# Revit family: OPTIMA_Compact_P_MM_DN15_2,5_RFA_2019
name_source: partatom
category: Pipe Accessories
units: mm (PartAtom-declared; Revit-internal decimal feet)

## family parameters
Always vertical = Yes
Cut with Voids When Loaded = No
Part Type = Valve - Breaks Into
Round Connector Dimension = Use Diameter
Shared = No
Work Plane-Based = No

## types (4) — shared parameters
BBVIS = No
CAT = No
Description = Armatura pro regulaci průtoku, omezení průtoku a stabilizaci tlakové diference
ENBL350 = No
H = 83 mm  [stored 0.27231 ft]
HH = 80 mm  [stored 0.262467 ft]
L = 36 mm  [stored 0.11811 ft]
L2 = 44 mm
L2D = 36 mm  [stored 0.11811 ft]
L2D_Min = 30 mm  [stored 0.0984252 ft]
L3 = 19 mm  [stored 0.062336 ft]
L4 = 13 mm  [stored 0.0426509 ft]
LLDAndHLD = Yes
LLDONLY = Yes
MC Enable LOD 200 = No
MC Enable LOD 350 = No
Manufacturer = Hydronic Systems Prague s.r.o.
QmdConnectorList = 301;D;302;D
R2 = 19 mm  [stored 0.062336 ft]
R2__ve = -19 mm  [stored -0.062336 ft]
R3 = 11 mm
R4 = 13 mm  [stored 0.0426509 ft]
R5 = 14 mm  [stored 0.0459318 ft]
R7 = 5 mm  [stored 0.0164042 ft]
Type Comments = vnější závit; PN25; 0~120°C, dpmax=800kPa; bez měřicích vsuvek
URL = www.hydronic.cz
VIS0 = No
Z1 = 17 mm
Z2 = 8 mm  [stored 0.0262467 ft]
Z3 = 13 mm  [stored 0.0426509 ft]
Z4 = 18 mm
Z6 = 5 mm  [stored 0.0164042 ft]
magiPartTypeId = 304
magiProductFamilyId = 5ce2593e541b4756b7958a6220b877

## per-type parameters (varying)
| type | D | DT2 | MC Product Code | R1 | TL | TLT2 | W2D | X1 | X2 | Z5 | magiProductId |
| OPTIMA Compact P DN15 M-M 2.5mm | 15 mm | 8 mm  [stored 0.0262467 ft] | 53-4100  (1/2" M-M; 2.5mm; Qmin~Qmax při dps=5kPa = 93~482 l/h; Qmin~Qmax při dps=10kPa = 73~378 l/h; kvs=1,3) | 7 mm  [stored 0.0229659 ft] | 65 mm  [stored 0.213255 ft] | 33 mm | 15 mm  [stored 0.0492126 ft] | 15 mm  [stored 0.0492126 ft] | 11 mm | 89 mm | e2c6e2867cb04e20b310fc655d8e25 |
| OPTIMA Compact P DN15 M-M 5.0mm | 15 mm | 8 mm  [stored 0.0262467 ft] | 53-4102  (1/2" M-M; 5.0mm; Qmin~Qmax při dps=5kPa = 198~1032 l/h; Qmin~Qmax při dps=10kPa = 156~809 l/h; kvs=2,7) | 7 mm  [stored 0.0229659 ft] | 65 mm  [stored 0.213255 ft] | 33 mm | 15 mm  [stored 0.0492126 ft] | 15 mm  [stored 0.0492126 ft] | 11 mm | 89 mm | de010cba6d924babace2e100200bd1 |
| OPTIMA Compact P DN20 M-M 2.5mm | 20 mm | 10 mm  [stored 0.0328084 ft] | 53-4103  (3/4" M-M; 2.5mm; Qmin~Qmax při dps=5kPa = 93~482 l/h; Qmin~Qmax při dps=10kPa = 73~378 l/h; kvs=1,3) | 9 mm  [stored 0.0295276 ft] | 70 mm  [stored 0.229659 ft] | 35 mm  [stored 0.114829 ft] | 20 mm  [stored 0.0656168 ft] | 17 mm | 13 mm  [stored 0.0426509 ft] | 91 mm  [stored 0.298556 ft] | 9b3b796f370b421c8a31739fcad6d9 |
| OPTIMA Compact P DN20 M-M 5.0mm | 20 mm | 10 mm  [stored 0.0328084 ft] | 53-4105  (3/4" M-M; 5.0mm; Qmin~Qmax při dps=5kPa = 198~1032 l/h; Qmin~Qmax při dps=10kPa = 156~809 l/h; kvs=2,7) | 9 mm  [stored 0.0295276 ft] | 70 mm  [stored 0.229659 ft] | 35 mm  [stored 0.114829 ft] | 20 mm  [stored 0.0656168 ft] | 17 mm | 13 mm  [stored 0.0426509 ft] | 91 mm  [stored 0.298556 ft] | 2f6d325ab3f64974a2f7ca30c30193 |

note: [stored X ft] marks values corroborated as IEEE doubles in the binary element streams (Revit-internal decimal feet)

## geometry (parser evidence)
native form markers: Sweep x12
no freeform markers — native parametric forms only
